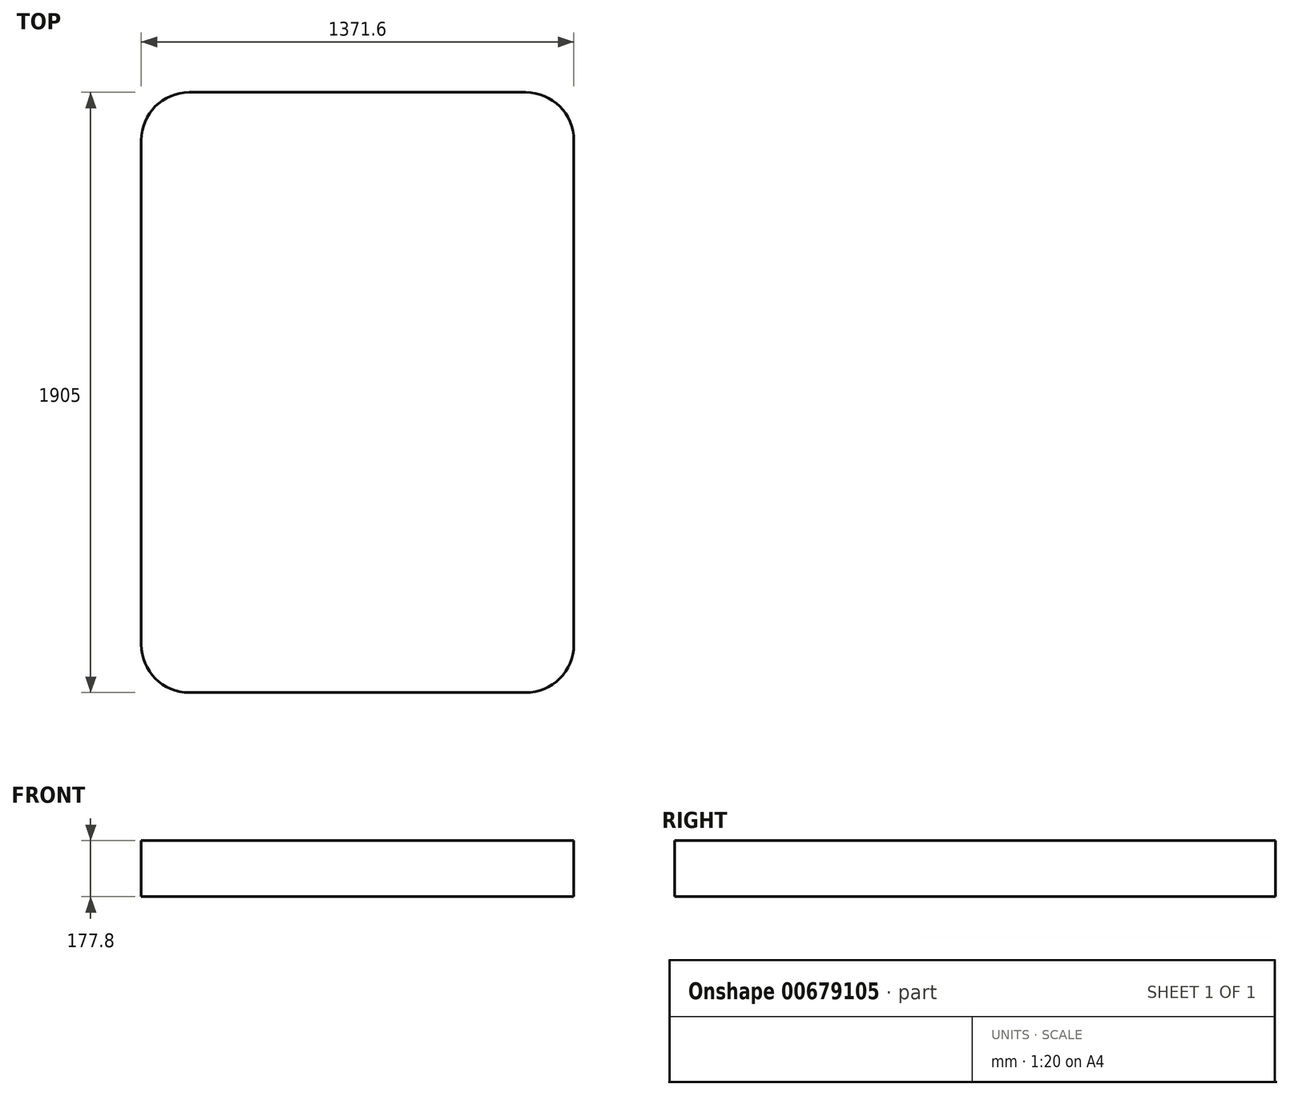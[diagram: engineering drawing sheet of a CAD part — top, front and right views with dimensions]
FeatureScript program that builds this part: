
annotation { "Feature Type Name" : "Feature", "Feature Type Description" : "" }
export const myFeature = defineFeature(function(context is Context, id is Id, definition is map)
    precondition{}
    {
        {
            var Q0;
            Q0=qCreatedBy(makeId("Top.planeOp"),FACE);
            var sketch = newSketch(context, id + "F0", { "sketchPlane" : qUnion([Q0])});
            skLineSegment(sketch, "E0.bottom", {"start": v(-534.47, 1263.64) * mm, "end": v(532.33, 1263.64) * mm});
            skLineSegment(sketch, "E0.top", {"start": v(-534.47, -641.36) * mm, "end": v(532.33, -641.36) * mm});
            skLineSegment(sketch, "E0.left", {"start": v(-686.87, 1111.24) * mm, "end": v(-686.87, -488.96) * mm});
            skLineSegment(sketch, "E0.right", {"start": v(684.73, 1111.24) * mm, "end": v(684.73, -488.96) * mm});
            skPoint(sketch, "E1.visualSharp", {"position": v(-686.87, -641.36) * mm});
            skArc(sketch, "E1.filletArc", {"start": v(-686.87, -488.96) * mm, "mid": v(-642.23, -596.73) * mm, "end": v(-534.47, -641.36) * mm});
            skPoint(sketch, "E2.visualSharp", {"position": v(684.73, -641.36) * mm});
            skArc(sketch, "E2.filletArc", {"start": v(532.33, -641.36) * mm, "mid": v(640.1, -596.73) * mm, "end": v(684.73, -488.96) * mm});
            skPoint(sketch, "E3.visualSharp", {"position": v(684.73, 1263.64) * mm});
            skArc(sketch, "E3.filletArc", {"start": v(684.73, 1111.24) * mm, "mid": v(640.1, 1219) * mm, "end": v(532.33, 1263.64) * mm});
            skPoint(sketch, "E4.visualSharp", {"position": v(-686.87, 1263.64) * mm});
            skArc(sketch, "E4.filletArc", {"start": v(-534.47, 1263.64) * mm, "mid": v(-642.23, 1219) * mm, "end": v(-686.87, 1111.24) * mm});
            skSolve(sketch);
        }
        {
            var Q0;
            Q0=makeQuery(id+"F0.imprint","IMPRINT",FACE,{"disambiguationData":[TD([[makeQuery(id+"F0.imprint","IMPRINT",EDGE,{"derivedFrom":sQuery(id+"F0.wireOp",EDGE,"E0.bottom")}),-1.0]])]});
            extrude(context, id + "F1", {"entities" : qUnion([Q0]), "depth" : 177.8 * mm, "offsetDistance" : 25.4 * mm});
        }
    });
